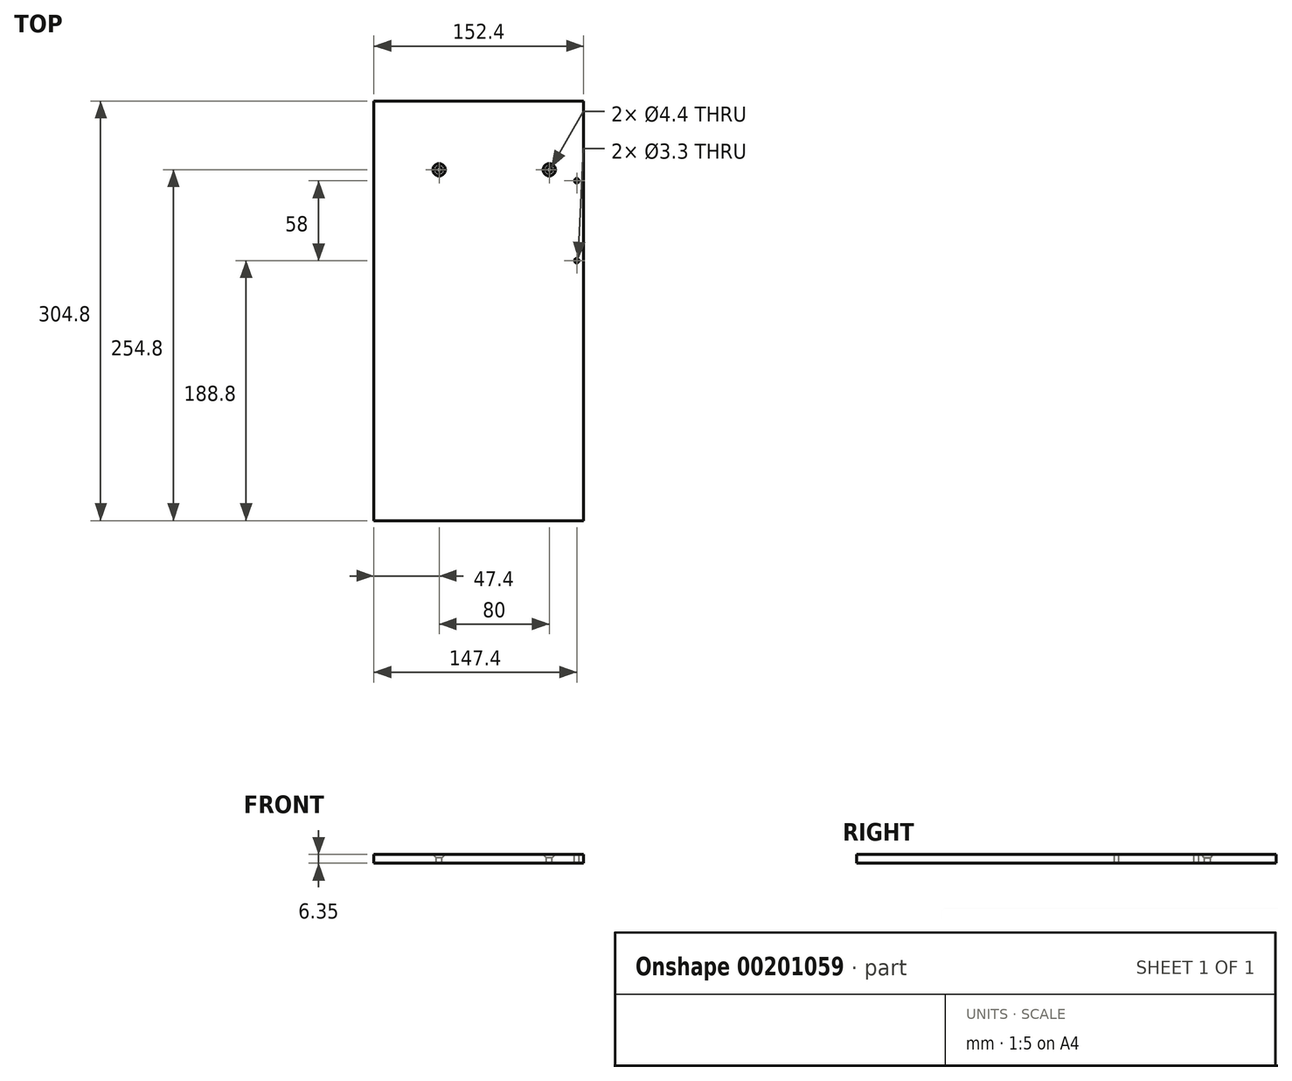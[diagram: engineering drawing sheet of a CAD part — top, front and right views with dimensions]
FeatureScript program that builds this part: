
annotation { "Feature Type Name" : "Feature", "Feature Type Description" : "" }
export const myFeature = defineFeature(function(context is Context, id is Id, definition is map)
    precondition{}
    {
        {
            var Q0;
            Q0=qCreatedBy(makeId("Top.planeOp"),FACE);
            var sketch = newSketch(context, id + "F0", { "sketchPlane" : qUnion([Q0])});
            skLineSegment(sketch, "E0.bottom", {"start": v(0, 0) * mm, "end": v(152.4, 0) * mm});
            skLineSegment(sketch, "E0.top", {"start": v(0, 304.8) * mm, "end": v(152.4, 304.8) * mm});
            skLineSegment(sketch, "E0.left", {"start": v(0, 0) * mm, "end": v(0, 304.8) * mm});
            skLineSegment(sketch, "E0.right", {"start": v(152.4, 0) * mm, "end": v(152.4, 304.8) * mm});
            skSolve(sketch);
        }
        {
            var Q0;
            Q0=qSketchRegion(id+"F0",true);
            extrude(context, id + "F1", {"entities" : qUnion([Q0]), "oppositeDirection" : true, "depth" : 6.35 * mm});
        }
        {
            var Q0;
            Q0=makeQuery(id+"F1.opExtrude","CAP_FACE",FACE,{"disambiguationData":[OSD([sQuery(id+"F0.wireOp",EDGE,"E0.bottom"),sQuery(id+"F0.wireOp",EDGE,"E0.top"),sQuery(id+"F0.wireOp",EDGE,"E0.left"),sQuery(id+"F0.wireOp",EDGE,"E0.right")])],"isStart":true});
            var sketch = newSketch(context, id + "F2", { "sketchPlane" : qUnion([Q0])});
            skPoint(sketch, "E1", {"position": v(47.4, 254.8) * mm});
            skPoint(sketch, "E2", {"position": v(127.4, 254.8) * mm});
            skSolve(sketch);
        }
        {
            var Q0;
            Q0=sQuery(id+"F2.wireOp",VERTEX,"E2");
            var Q1;
            Q1=sQuery(id+"F2.wireOp",VERTEX,"E1");
            var Q2;
            Q2=makeQuery(id+"F1.opExtrude","SWEPT_BODY",BODY,{"disambiguationData":[OSD([sQuery(id+"F0.wireOp",EDGE,"E0.bottom"),sQuery(id+"F0.wireOp",EDGE,"E0.top"),sQuery(id+"F0.wireOp",EDGE,"E0.left"),sQuery(id+"F0.wireOp",EDGE,"E0.right")])]});
            hole(context, id + "F3", {"style" : HoleStyle.C_SINK, "endStyle" : HoleEndStyle.THROUGH, "standardTappedOrClearance" : lookupTablePath({ "standard" : "ISO", "fit" : "Normal", "size" : "M4", "type" : "Clearance" }), "standardBlindInLast" : lookupTablePath({ "fit" : "Standard", "standard" : "ISO", "size" : "M4", "type" : "Clearance" }), "holeDiameter" : 4.4 * mm, "cSinkDiameter" : 8.96 * mm, "cSinkAngle" : 90 * degree, "locations" : qUnion([Q0, Q1]), "scope" : qUnion([Q2]), "isTappedThrough" : true});
        }
        {
            var Q0;
            Q0=makeQuery(id+"F1.opExtrude","CAP_FACE",FACE,{"disambiguationData":[OSD([sQuery(id+"F0.wireOp",EDGE,"E0.bottom"),sQuery(id+"F0.wireOp",EDGE,"E0.top"),sQuery(id+"F0.wireOp",EDGE,"E0.left"),sQuery(id+"F0.wireOp",EDGE,"E0.right")])],"isStart":true});
            var sketch = newSketch(context, id + "F4", { "sketchPlane" : qUnion([Q0])});
            skPoint(sketch, "E3", {"position": v(147.4, 246.8) * mm});
            skPoint(sketch, "E4", {"position": v(147.4, 188.8) * mm});
            skSolve(sketch);
        }
        {
            var Q0;
            Q0=sQuery(id+"F4.wireOp",VERTEX,"E3");
            var Q1;
            Q1=sQuery(id+"F4.wireOp",VERTEX,"E4");
            var Q2;
            Q2=makeQuery(id+"F1.opExtrude","SWEPT_BODY",BODY,{"disambiguationData":[OSD([sQuery(id+"F0.wireOp",EDGE,"E0.bottom"),sQuery(id+"F0.wireOp",EDGE,"E0.top"),sQuery(id+"F0.wireOp",EDGE,"E0.left"),sQuery(id+"F0.wireOp",EDGE,"E0.right")])]});
            hole(context, id + "F5", {"style" : HoleStyle.SIMPLE, "endStyle" : HoleEndStyle.THROUGH, "standardTappedOrClearance" : lookupTablePath({ "standard" : "ISO", "engagement" : "75%", "pitch" : "0.7 mm", "size" : "M4", "type" : "Tapped" }), "standardBlindInLast" : lookupTablePath({ "standard" : "ISO", "engagement" : "75%", "pitch" : "0.7 mm", "size" : "M4", "type" : "Tapped" }), "holeDiameter" : 3.3 * mm, "locations" : qUnion([Q0, Q1]), "scope" : qUnion([Q2]), "isTappedThrough" : true, "majorDiameter" : 4 * mm, "showTappedDepth" : true});
        }
    });
